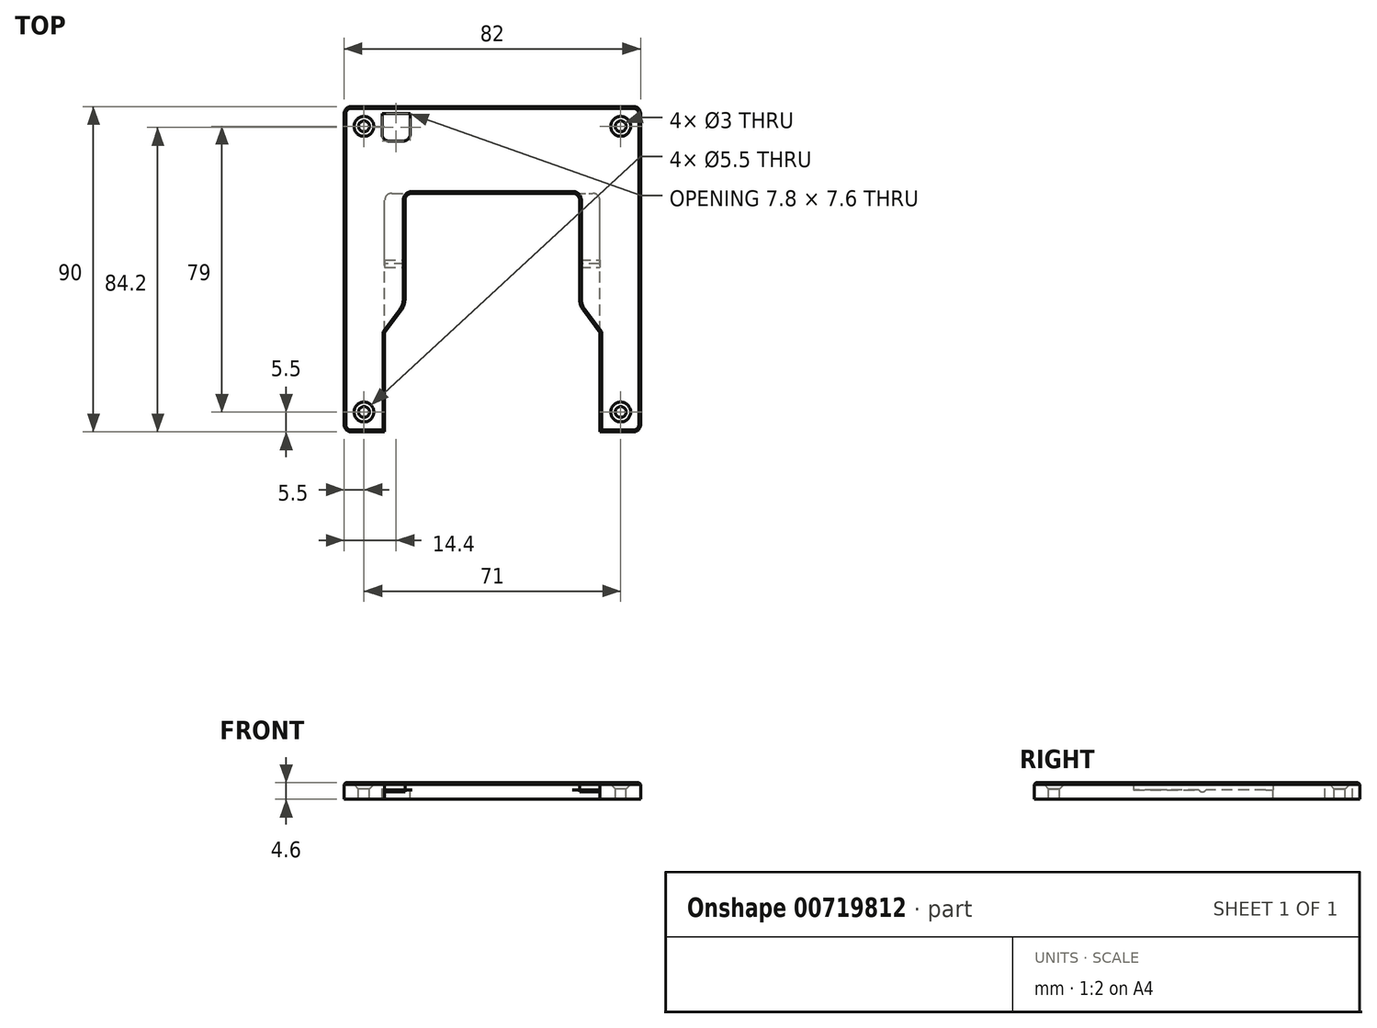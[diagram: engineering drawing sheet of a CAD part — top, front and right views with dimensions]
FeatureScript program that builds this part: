
annotation { "Feature Type Name" : "Feature", "Feature Type Description" : "" }
export const myFeature = defineFeature(function(context is Context, id is Id, definition is map)
    precondition{}
    {
        {
            var Q0;
            Q0=qCreatedBy(makeId("Top.planeOp"),FACE);
            var sketch = newSketch(context, id + "F0", { "sketchPlane" : qUnion([Q0])});
            skLineSegment(sketch, "E0.bottom", {"start": v(2, 0) * mm, "end": v(80, 0) * mm});
            skLineSegment(sketch, "E0.top", {"start": v(2, -90) * mm, "end": v(11.25, -90) * mm});
            skLineSegment(sketch, "E0.left", {"start": v(0, -2) * mm, "end": v(0, -88) * mm});
            skLineSegment(sketch, "E0.right", {"start": v(82, -2) * mm, "end": v(82, -88) * mm});
            skPoint(sketch, "E1.visualSharp", {"position": v(0, 0) * mm});
            skArc(sketch, "E1.filletArc", {"start": v(2, 0) * mm, "mid": v(0.59, -0.59) * mm, "end": v(0, -2) * mm});
            skPoint(sketch, "E2.visualSharp", {"position": v(82, 0) * mm});
            skArc(sketch, "E2.filletArc", {"start": v(82, -2) * mm, "mid": v(81.41, -0.59) * mm, "end": v(80, 0) * mm});
            skPoint(sketch, "E3.visualSharp", {"position": v(82, -90) * mm});
            skArc(sketch, "E3.filletArc", {"start": v(80, -90) * mm, "mid": v(81.41, -89.41) * mm, "end": v(82, -88) * mm});
            skPoint(sketch, "E4.visualSharp", {"position": v(0, -90) * mm});
            skArc(sketch, "E4.filletArc", {"start": v(0, -88) * mm, "mid": v(0.59, -89.41) * mm, "end": v(2, -90) * mm});
            skLineSegment(sketch, "E5.top", {"start": v(18.85, -24) * mm, "end": v(63.15, -24) * mm});
            skLineSegment(sketch, "E5.left", {"start": v(11.25, -90) * mm, "end": v(11.25, -62.5) * mm});
            skLineSegment(sketch, "E5.right", {"start": v(70.75, -90) * mm, "end": v(70.75, -62.5) * mm});
            skLineSegment(sketch, "E6.trimOffspring", {"start": v(70.75, -90) * mm, "end": v(80, -90) * mm});
            skLineSegment(sketch, "E7.right", {"start": v(16.85, -26) * mm, "end": v(16.85, -53.34) * mm});
            skLineSegment(sketch, "E8.right", {"start": v(65.15, -26) * mm, "end": v(65.15, -53.34) * mm});
            skPoint(sketch, "E9.visualSharp", {"position": v(16.85, -24) * mm});
            skArc(sketch, "E9.filletArc", {"start": v(18.85, -24) * mm, "mid": v(17.44, -24.59) * mm, "end": v(16.85, -26) * mm});
            skPoint(sketch, "E10.visualSharp", {"position": v(65.15, -24) * mm});
            skArc(sketch, "E10.filletArc", {"start": v(65.15, -26) * mm, "mid": v(64.56, -24.59) * mm, "end": v(63.15, -24) * mm});
            skPoint(sketch, "E11", {"position": v(16.85, -55) * mm});
            skLineSegment(sketch, "E12", {"start": v(11.25, -62.5) * mm, "end": v(15.86, -56.33) * mm});
            skLineSegment(sketch, "E13", {"start": v(66.14, -56.33) * mm, "end": v(70.75, -62.5) * mm});
            skArc(sketch, "E14.filletArc", {"start": v(15.86, -56.33) * mm, "mid": v(16.6, -54.92) * mm, "end": v(16.85, -53.34) * mm});
            skPoint(sketch, "E15.visualSharp", {"position": v(65.15, -55) * mm});
            skArc(sketch, "E15.filletArc", {"start": v(65.15, -53.34) * mm, "mid": v(65.4, -54.92) * mm, "end": v(66.14, -56.33) * mm});
            skSolve(sketch);
        }
        {
            var Q0;
            Q0=makeQuery(id+"F0.imprint","IMPRINT",FACE,{"disambiguationData":[TD([[makeQuery(id+"F0.imprint","IMPRINT",EDGE,{"derivedFrom":sQuery(id+"F0.wireOp",EDGE,"E0.bottom")}),-1.0]])]});
            extrude(context, id + "F1", {"entities" : qUnion([Q0]), "depth" : 2 * mm, "offsetDistance" : 25 * mm});
        }
        {
            var Q0;
            Q0=makeQuery(id+"F1.opExtrude","CAP_FACE",FACE,{"disambiguationData":[OSD([sQuery(id+"F0.wireOp",EDGE,"E0.bottom"),sQuery(id+"F0.wireOp",EDGE,"E0.top"),sQuery(id+"F0.wireOp",EDGE,"E0.left"),sQuery(id+"F0.wireOp",EDGE,"E0.right"),sQuery(id+"F0.wireOp",EDGE,"E1.filletArc"),sQuery(id+"F0.wireOp",EDGE,"E2.filletArc"),sQuery(id+"F0.wireOp",EDGE,"E3.filletArc"),sQuery(id+"F0.wireOp",EDGE,"E4.filletArc"),sQuery(id+"F0.wireOp",EDGE,"E5.top"),sQuery(id+"F0.wireOp",EDGE,"E5.left"),sQuery(id+"F0.wireOp",EDGE,"E5.right"),sQuery(id+"F0.wireOp",EDGE,"E6.trimOffspring"),sQuery(id+"F0.wireOp",EDGE,"E7.right"),sQuery(id+"F0.wireOp",EDGE,"E8.right"),sQuery(id+"F0.wireOp",EDGE,"E9.filletArc"),sQuery(id+"F0.wireOp",EDGE,"E10.filletArc"),sQuery(id+"F0.wireOp",EDGE,"E12"),sQuery(id+"F0.wireOp",EDGE,"E13"),sQuery(id+"F0.wireOp",EDGE,"E14.filletArc"),sQuery(id+"F0.wireOp",EDGE,"E15.filletArc")])],"isStart":true});
            var sketch = newSketch(context, id + "F2", { "sketchPlane" : qUnion([Q0])});
            skArc(sketch, "E16.0", {"start": v(82, 2) * mm, "mid": v(81.41, 0.59) * mm, "end": v(80, 0) * mm});
            skLineSegment(sketch, "E16.1", {"start": v(2, 0) * mm, "end": v(80, 0) * mm});
            skArc(sketch, "E16.2", {"start": v(2, 0) * mm, "mid": v(0.59, 0.59) * mm, "end": v(0, 2) * mm});
            skLineSegment(sketch, "E16.3", {"start": v(0, 2) * mm, "end": v(0, 88) * mm});
            skArc(sketch, "E16.4", {"start": v(0, 88) * mm, "mid": v(0.59, 89.41) * mm, "end": v(2, 90) * mm});
            skLineSegment(sketch, "E16.5", {"start": v(82, 2) * mm, "end": v(82, 88) * mm});
            skLineSegment(sketch, "E16.6", {"start": v(2, 90) * mm, "end": v(11.25, 90) * mm});
            skLineSegment(sketch, "E16.7", {"start": v(11.25, 90) * mm, "end": v(11.25, 62.5) * mm});
            skLineSegment(sketch, "E16.9", {"start": v(70.75, 90) * mm, "end": v(70.75, 62.5) * mm});
            skLineSegment(sketch, "E16.10", {"start": v(70.75, 90) * mm, "end": v(80, 90) * mm});
            skArc(sketch, "E16.11", {"start": v(80, 90) * mm, "mid": v(81.41, 89.41) * mm, "end": v(82, 88) * mm});
            skLineSegment(sketch, "E16.14", {"start": v(16.85, 24) * mm, "end": v(65.15, 24) * mm});
            skLineSegment(sketch, "E17", {"start": v(70.75, 62.5) * mm, "end": v(70.75, 26) * mm});
            skLineSegment(sketch, "E18", {"start": v(68.75, 24) * mm, "end": v(65.15, 24) * mm});
            skPoint(sketch, "E19.visualSharp", {"position": v(70.75, 24) * mm});
            skArc(sketch, "E19.filletArc", {"start": v(68.75, 24) * mm, "mid": v(70.16, 24.59) * mm, "end": v(70.75, 26) * mm});
            skLineSegment(sketch, "E20", {"start": v(11.25, 62.5) * mm, "end": v(11.25, 26) * mm});
            skLineSegment(sketch, "E21", {"start": v(13.25, 24) * mm, "end": v(16.85, 24) * mm});
            skPoint(sketch, "E22.visualSharp", {"position": v(11.25, 24) * mm});
            skArc(sketch, "E22.filletArc", {"start": v(11.25, 26) * mm, "mid": v(11.84, 24.59) * mm, "end": v(13.25, 24) * mm});
            skSolve(sketch);
        }
        {
            var Q0;
            Q0 = qSketchRegion(id + "F2", true);
            extrude(context, id + "F3", {"entities" : qUnion([Q0]), "operationType" : NewBodyOperationType.ADD, "depth" : 2.2 * mm, "offsetDistance" : 25 * mm});
        }
        {
            var Q0;
            Q0=makeQuery(id+"F1.opExtrude","CAP_FACE",FACE,{"disambiguationData":[OSD([sQuery(id+"F0.wireOp",EDGE,"E0.bottom"),sQuery(id+"F0.wireOp",EDGE,"E0.top"),sQuery(id+"F0.wireOp",EDGE,"E0.left"),sQuery(id+"F0.wireOp",EDGE,"E0.right"),sQuery(id+"F0.wireOp",EDGE,"E1.filletArc"),sQuery(id+"F0.wireOp",EDGE,"E2.filletArc"),sQuery(id+"F0.wireOp",EDGE,"E3.filletArc"),sQuery(id+"F0.wireOp",EDGE,"E4.filletArc"),sQuery(id+"F0.wireOp",EDGE,"E5.top"),sQuery(id+"F0.wireOp",EDGE,"E5.left"),sQuery(id+"F0.wireOp",EDGE,"E5.right"),sQuery(id+"F0.wireOp",EDGE,"E6.trimOffspring"),sQuery(id+"F0.wireOp",EDGE,"E7.right"),sQuery(id+"F0.wireOp",EDGE,"E8.right"),sQuery(id+"F0.wireOp",EDGE,"E9.filletArc"),sQuery(id+"F0.wireOp",EDGE,"E10.filletArc"),sQuery(id+"F0.wireOp",EDGE,"E12"),sQuery(id+"F0.wireOp",EDGE,"E13"),sQuery(id+"F0.wireOp",EDGE,"E14.filletArc"),sQuery(id+"F0.wireOp",EDGE,"E15.filletArc")])],"isStart":false});
            var sketch = newSketch(context, id + "F4", { "sketchPlane" : qUnion([Q0])});
            skLineSegment(sketch, "E23.bottom", {"start": v(10.5, -2) * mm, "end": v(18.3, -2) * mm});
            skLineSegment(sketch, "E23.top", {"start": v(12.5, -9.6) * mm, "end": v(16.3, -9.6) * mm});
            skLineSegment(sketch, "E23.left", {"start": v(10.5, -2) * mm, "end": v(10.5, -7.6) * mm});
            skLineSegment(sketch, "E23.right", {"start": v(18.3, -2) * mm, "end": v(18.3, -7.6) * mm});
            skPoint(sketch, "E24.visualSharp", {"position": v(10.5, -9.6) * mm});
            skArc(sketch, "E24.filletArc", {"start": v(10.5, -7.6) * mm, "mid": v(11.09, -9.01) * mm, "end": v(12.5, -9.6) * mm});
            skPoint(sketch, "E25.visualSharp", {"position": v(18.3, -9.6) * mm});
            skArc(sketch, "E25.filletArc", {"start": v(16.3, -9.6) * mm, "mid": v(17.71, -9.01) * mm, "end": v(18.3, -7.6) * mm});
            skSolve(sketch);
        }
        {
            var Q0;
            Q0 = qSketchRegion(id + "F4", true);
            extrude(context, id + "F5", {"entities" : qUnion([Q0]), "operationType" : NewBodyOperationType.REMOVE, "oppositeDirection" : true, "depth" : 25 * mm, "offsetDistance" : 25 * mm});
        }
        {
            var Q0;
            Q0=makeQuery(id+"F1.opExtrude","CAP_FACE",FACE,{"disambiguationData":[OSD([sQuery(id+"F0.wireOp",EDGE,"E0.bottom"),sQuery(id+"F0.wireOp",EDGE,"E0.top"),sQuery(id+"F0.wireOp",EDGE,"E0.left"),sQuery(id+"F0.wireOp",EDGE,"E0.right"),sQuery(id+"F0.wireOp",EDGE,"E1.filletArc"),sQuery(id+"F0.wireOp",EDGE,"E2.filletArc"),sQuery(id+"F0.wireOp",EDGE,"E3.filletArc"),sQuery(id+"F0.wireOp",EDGE,"E4.filletArc"),sQuery(id+"F0.wireOp",EDGE,"E5.top"),sQuery(id+"F0.wireOp",EDGE,"E5.left"),sQuery(id+"F0.wireOp",EDGE,"E5.right"),sQuery(id+"F0.wireOp",EDGE,"E6.trimOffspring"),sQuery(id+"F0.wireOp",EDGE,"E7.right"),sQuery(id+"F0.wireOp",EDGE,"E8.right"),sQuery(id+"F0.wireOp",EDGE,"E9.filletArc"),sQuery(id+"F0.wireOp",EDGE,"E10.filletArc"),sQuery(id+"F0.wireOp",EDGE,"E12"),sQuery(id+"F0.wireOp",EDGE,"E13"),sQuery(id+"F0.wireOp",EDGE,"E14.filletArc"),sQuery(id+"F0.wireOp",EDGE,"E15.filletArc")])],"isStart":false});
            var sketch = newSketch(context, id + "F6", { "sketchPlane" : qUnion([Q0])});
            skCircle(sketch, "E26", {"center": v(5.5, -5.5) * mm, "radius": 1.5 * mm});
            skCircle(sketch, "E27", {"center": v(76.5, -5.5) * mm, "radius": 1.5 * mm});
            skCircle(sketch, "E28", {"center": v(5.5, -84.5) * mm, "radius": 1.5 * mm});
            skCircle(sketch, "E29", {"center": v(76.5, -84.5) * mm, "radius": 1.5 * mm});
            skSolve(sketch);
        }
        {
            var Q0;
            Q0=makeQuery(id+"F6.imprint","IMPRINT",FACE,{"disambiguationData":[TD([[makeQuery(id+"F6.imprint","IMPRINT",EDGE,{"derivedFrom":sQuery(id+"F6.wireOp",EDGE,"E28")}),1.0]])]});
            var Q1;
            Q1=makeQuery(id+"F6.imprint","IMPRINT",FACE,{"disambiguationData":[TD([[makeQuery(id+"F6.imprint","IMPRINT",EDGE,{"derivedFrom":sQuery(id+"F6.wireOp",EDGE,"E29")}),1.0]])]});
            var Q2;
            Q2=makeQuery(id+"F6.imprint","IMPRINT",FACE,{"disambiguationData":[TD([[makeQuery(id+"F6.imprint","IMPRINT",EDGE,{"derivedFrom":sQuery(id+"F6.wireOp",EDGE,"E26")}),1.0]])]});
            var Q3;
            Q3=makeQuery(id+"F6.imprint","IMPRINT",FACE,{"disambiguationData":[TD([[makeQuery(id+"F6.imprint","IMPRINT",EDGE,{"derivedFrom":sQuery(id+"F6.wireOp",EDGE,"E27")}),1.0]])]});
            extrude(context, id + "F7", {"entities" : qUnion([Q0, Q1, Q2, Q3]), "operationType" : NewBodyOperationType.REMOVE, "oppositeDirection" : true, "depth" : 4.2 * mm, "offsetDistance" : 25 * mm});
        }
        {
            var Q0;
            Q0=makeQuery(id+"F1.opExtrude","CAP_FACE",FACE,{"disambiguationData":[OSD([sQuery(id+"F0.wireOp",EDGE,"E0.bottom"),sQuery(id+"F0.wireOp",EDGE,"E0.top"),sQuery(id+"F0.wireOp",EDGE,"E0.left"),sQuery(id+"F0.wireOp",EDGE,"E0.right"),sQuery(id+"F0.wireOp",EDGE,"E1.filletArc"),sQuery(id+"F0.wireOp",EDGE,"E2.filletArc"),sQuery(id+"F0.wireOp",EDGE,"E3.filletArc"),sQuery(id+"F0.wireOp",EDGE,"E4.filletArc"),sQuery(id+"F0.wireOp",EDGE,"E5.top"),sQuery(id+"F0.wireOp",EDGE,"E5.left"),sQuery(id+"F0.wireOp",EDGE,"E5.right"),sQuery(id+"F0.wireOp",EDGE,"E6.trimOffspring"),sQuery(id+"F0.wireOp",EDGE,"E7.right"),sQuery(id+"F0.wireOp",EDGE,"E8.right"),sQuery(id+"F0.wireOp",EDGE,"E9.filletArc"),sQuery(id+"F0.wireOp",EDGE,"E10.filletArc"),sQuery(id+"F0.wireOp",EDGE,"E12"),sQuery(id+"F0.wireOp",EDGE,"E13"),sQuery(id+"F0.wireOp",EDGE,"E14.filletArc"),sQuery(id+"F0.wireOp",EDGE,"E15.filletArc")])],"isStart":false});
            var sketch = newSketch(context, id + "F8", { "sketchPlane" : qUnion([Q0])});
            skCircle(sketch, "E30", {"center": v(5.5, -5.5) * mm, "radius": 2.75 * mm});
            skCircle(sketch, "E31", {"center": v(76.5, -5.5) * mm, "radius": 2.75 * mm});
            skCircle(sketch, "E32", {"center": v(76.5, -84.5) * mm, "radius": 2.75 * mm});
            skCircle(sketch, "E33", {"center": v(5.5, -84.5) * mm, "radius": 2.75 * mm});
            skSolve(sketch);
        }
        {
            var Q0;
            Q0 = qSketchRegion(id + "F8", true);
            extrude(context, id + "F9", {"entities" : qUnion([Q0]), "operationType" : NewBodyOperationType.REMOVE, "oppositeDirection" : true, "depth" : 2 * mm, "offsetDistance" : 25 * mm});
        }
        {
            var Q0;
            Q0=makeQuery(id+"F9.boolean.opBoolean","COPY",EDGE,{"derivedFrom":makeQuery(id+"F9.opExtrude","CAP_EDGE",EDGE,{"disambiguationData":[OSD([sQuery(id+"F8.wireOp",EDGE,"E33")])],"isStart":false})});
            var Q1;
            Q1=makeQuery(id+"F9.boolean.opBoolean","COPY",EDGE,{"derivedFrom":makeQuery(id+"F9.opExtrude","CAP_EDGE",EDGE,{"disambiguationData":[OSD([sQuery(id+"F8.wireOp",EDGE,"E32")])],"isStart":false})});
            var Q2;
            Q2=makeQuery(id+"F9.boolean.opBoolean","COPY",EDGE,{"derivedFrom":makeQuery(id+"F9.opExtrude","CAP_EDGE",EDGE,{"disambiguationData":[OSD([sQuery(id+"F8.wireOp",EDGE,"E30")])],"isStart":false})});
            var Q3;
            Q3=makeQuery(id+"F9.boolean.opBoolean","COPY",EDGE,{"derivedFrom":makeQuery(id+"F9.opExtrude","CAP_EDGE",EDGE,{"disambiguationData":[OSD([sQuery(id+"F8.wireOp",EDGE,"E31")])],"isStart":false})});
            chamfer(context, id + "F10", {"entities" : qUnion([Q0, Q1, Q2, Q3]), "width" : 1.5 * mm, "tangentPropagation" : true});
        }
        {
            var Q0;
            {var subQ0=sQuery(id+"F0.wireOp",EDGE,"E7.right");var subQ1=sQuery(id+"F0.wireOp",EDGE,"E9.filletArc");var subQ2=sQuery(id+"F0.wireOp",EDGE,"E5.left");var subQ3=sQuery(id+"F0.wireOp",EDGE,"E5.top");var subQ4=sQuery(id+"F0.wireOp",EDGE,"E12");var subQ5=sQuery(id+"F0.wireOp",EDGE,"E14.filletArc");Q0=makeQuery(id+"F3.boolean.opBoolean","SPLIT",FACE,{"disambiguationData":[TD([makeQuery(id+"F1.opExtrude","SWEPT_FACE",FACE,{"disambiguationData":[OSD([subQ2])]})])],"derivedFrom":makeQuery(id+"F1.opExtrude","CAP_FACE",FACE,{"disambiguationData":[OSD([sQuery(id+"F0.wireOp",EDGE,"E0.bottom"),sQuery(id+"F0.wireOp",EDGE,"E0.top"),sQuery(id+"F0.wireOp",EDGE,"E0.left"),sQuery(id+"F0.wireOp",EDGE,"E0.right"),sQuery(id+"F0.wireOp",EDGE,"E1.filletArc"),sQuery(id+"F0.wireOp",EDGE,"E2.filletArc"),sQuery(id+"F0.wireOp",EDGE,"E3.filletArc"),sQuery(id+"F0.wireOp",EDGE,"E4.filletArc"),subQ3,subQ2,sQuery(id+"F0.wireOp",EDGE,"E5.right"),sQuery(id+"F0.wireOp",EDGE,"E6.trimOffspring"),subQ0,sQuery(id+"F0.wireOp",EDGE,"E8.right"),subQ1,sQuery(id+"F0.wireOp",EDGE,"E10.filletArc"),subQ4,sQuery(id+"F0.wireOp",EDGE,"E13"),subQ5,sQuery(id+"F0.wireOp",EDGE,"E15.filletArc")])],"isStart":true})});}
            var sketch = newSketch(context, id + "F11", { "sketchPlane" : qUnion([Q0])});
            skLineSegment(sketch, "E34.bottom", {"start": v(11.25, 44.5) * mm, "end": v(16.85, 44.5) * mm});
            skLineSegment(sketch, "E34.top", {"start": v(11.25, 42.5) * mm, "end": v(16.85, 42.5) * mm});
            skLineSegment(sketch, "E34.left", {"start": v(11.25, 44.5) * mm, "end": v(11.25, 42.5) * mm});
            skLineSegment(sketch, "E34.right", {"start": v(16.85, 44.5) * mm, "end": v(16.85, 42.5) * mm});
            skLineSegment(sketch, "E35.bottom", {"start": v(65.15, 42.5) * mm, "end": v(70.75, 42.5) * mm});
            skLineSegment(sketch, "E35.top", {"start": v(65.15, 44.5) * mm, "end": v(70.75, 44.5) * mm});
            skLineSegment(sketch, "E35.left", {"start": v(65.15, 42.5) * mm, "end": v(65.15, 44.5) * mm});
            skLineSegment(sketch, "E35.right", {"start": v(70.75, 42.5) * mm, "end": v(70.75, 44.5) * mm});
            skSolve(sketch);
        }
        {
            var Q0;
            Q0 = qSketchRegion(id + "F11", true);
            extrude(context, id + "F12", {"entities" : qUnion([Q0]), "operationType" : NewBodyOperationType.ADD, "depth" : 0.6 * mm, "offsetDistance" : 25 * mm});
        }
        {
            var Q0;
            Q0=makeQuery(id+"F12.opExtrude","CAP_EDGE",EDGE,{"disambiguationData":[OSD([sQuery(id+"F11.wireOp",EDGE,"E34.top")])],"isStart":false});
            var Q1;
            Q1=makeQuery(id+"F12.opExtrude","CAP_EDGE",EDGE,{"disambiguationData":[OSD([sQuery(id+"F11.wireOp",EDGE,"E34.bottom")])],"isStart":false});
            var Q2;
            Q2=makeQuery(id+"F12.opExtrude","CAP_EDGE",EDGE,{"disambiguationData":[OSD([sQuery(id+"F11.wireOp",EDGE,"E35.bottom")])],"isStart":false});
            var Q3;
            Q3=makeQuery(id+"F12.opExtrude","CAP_EDGE",EDGE,{"disambiguationData":[OSD([sQuery(id+"F11.wireOp",EDGE,"E35.top")])],"isStart":false});
            fillet(context, id + "F13", {"entities" : qUnion([Q0, Q1, Q2, Q3]), "radius" : 1.4 * mm, "tangentPropagation" : true, "allowEdgeOverflow" : false});
        }
        {
            var Q0;
            Q0=makeQuery(id+"F1.opExtrude","CAP_EDGE",EDGE,{"disambiguationData":[OSD([sQuery(id+"F0.wireOp",EDGE,"E1.filletArc")])],"isStart":false});
            var Q1;
            Q1=makeQuery(id+"F1.opExtrude","CAP_EDGE",EDGE,{"disambiguationData":[OSD([sQuery(id+"F0.wireOp",EDGE,"E0.bottom")])],"isStart":false});
            var Q2;
            Q2=makeQuery(id+"F1.opExtrude","CAP_EDGE",EDGE,{"disambiguationData":[OSD([sQuery(id+"F0.wireOp",EDGE,"E0.left")])],"isStart":false});
            var Q3;
            Q3=makeQuery(id+"F5.boolean.opBoolean","COPY",EDGE,{"derivedFrom":makeQuery(id+"F5.opExtrude","CAP_EDGE",EDGE,{"disambiguationData":[OSD([sQuery(id+"F4.wireOp",EDGE,"E23.left")])],"isStart":true})});
            var Q4;
            Q4=makeQuery(id+"F5.boolean.opBoolean","COPY",EDGE,{"derivedFrom":makeQuery(id+"F5.opExtrude","CAP_EDGE",EDGE,{"disambiguationData":[OSD([sQuery(id+"F4.wireOp",EDGE,"E23.bottom")])],"isStart":true})});
            var Q5;
            Q5=makeQuery(id+"F5.boolean.opBoolean","COPY",EDGE,{"derivedFrom":makeQuery(id+"F5.opExtrude","CAP_EDGE",EDGE,{"disambiguationData":[OSD([sQuery(id+"F4.wireOp",EDGE,"E23.right")])],"isStart":true})});
            var Q6;
            Q6=makeQuery(id+"F5.boolean.opBoolean","COPY",EDGE,{"derivedFrom":makeQuery(id+"F5.opExtrude","CAP_EDGE",EDGE,{"disambiguationData":[OSD([sQuery(id+"F4.wireOp",EDGE,"E25.filletArc")])],"isStart":true})});
            var Q7;
            Q7=makeQuery(id+"F5.boolean.opBoolean","COPY",EDGE,{"derivedFrom":makeQuery(id+"F5.opExtrude","CAP_EDGE",EDGE,{"disambiguationData":[OSD([sQuery(id+"F4.wireOp",EDGE,"E23.top")])],"isStart":true})});
            var Q8;
            Q8=makeQuery(id+"F5.boolean.opBoolean","COPY",EDGE,{"derivedFrom":makeQuery(id+"F5.opExtrude","CAP_EDGE",EDGE,{"disambiguationData":[OSD([sQuery(id+"F4.wireOp",EDGE,"E24.filletArc")])],"isStart":true})});
            var Q9;
            Q9=makeQuery(id+"F1.opExtrude","CAP_EDGE",EDGE,{"disambiguationData":[OSD([sQuery(id+"F0.wireOp",EDGE,"E2.filletArc")])],"isStart":false});
            var Q10;
            Q10=makeQuery(id+"F1.opExtrude","CAP_EDGE",EDGE,{"disambiguationData":[OSD([sQuery(id+"F0.wireOp",EDGE,"E0.right")])],"isStart":false});
            var Q11;
            Q11=makeQuery(id+"F1.opExtrude","CAP_EDGE",EDGE,{"disambiguationData":[OSD([sQuery(id+"F0.wireOp",EDGE,"E5.left")])],"isStart":false});
            var Q12;
            Q12=makeQuery(id+"F1.opExtrude","CAP_EDGE",EDGE,{"disambiguationData":[OSD([sQuery(id+"F0.wireOp",EDGE,"E0.top")])],"isStart":false});
            var Q13;
            Q13=makeQuery(id+"F1.opExtrude","CAP_EDGE",EDGE,{"disambiguationData":[OSD([sQuery(id+"F0.wireOp",EDGE,"E4.filletArc")])],"isStart":false});
            var Q14;
            Q14=makeQuery(id+"F1.opExtrude","CAP_EDGE",EDGE,{"disambiguationData":[OSD([sQuery(id+"F0.wireOp",EDGE,"E3.filletArc")])],"isStart":false});
            var Q15;
            Q15=makeQuery(id+"F1.opExtrude","CAP_EDGE",EDGE,{"disambiguationData":[OSD([sQuery(id+"F0.wireOp",EDGE,"E6.trimOffspring")])],"isStart":false});
            var Q16;
            Q16=makeQuery(id+"F1.opExtrude","CAP_EDGE",EDGE,{"disambiguationData":[OSD([sQuery(id+"F0.wireOp",EDGE,"E5.right")])],"isStart":false});
            var Q17;
            Q17=makeQuery(id+"F1.opExtrude","CAP_EDGE",EDGE,{"disambiguationData":[OSD([sQuery(id+"F0.wireOp",EDGE,"E13")])],"isStart":false});
            var Q18;
            Q18=makeQuery(id+"F1.opExtrude","CAP_EDGE",EDGE,{"disambiguationData":[OSD([sQuery(id+"F0.wireOp",EDGE,"E15.filletArc")])],"isStart":false});
            var Q19;
            Q19=makeQuery(id+"F1.opExtrude","CAP_EDGE",EDGE,{"disambiguationData":[OSD([sQuery(id+"F0.wireOp",EDGE,"E8.right")])],"isStart":false});
            var Q20;
            Q20=makeQuery(id+"F1.opExtrude","CAP_EDGE",EDGE,{"disambiguationData":[OSD([sQuery(id+"F0.wireOp",EDGE,"E10.filletArc")])],"isStart":false});
            var Q21;
            Q21=makeQuery(id+"F1.opExtrude","CAP_EDGE",EDGE,{"disambiguationData":[OSD([sQuery(id+"F0.wireOp",EDGE,"E5.top")])],"isStart":false});
            var Q22;
            Q22=makeQuery(id+"F1.opExtrude","CAP_EDGE",EDGE,{"disambiguationData":[OSD([sQuery(id+"F0.wireOp",EDGE,"E9.filletArc")])],"isStart":false});
            var Q23;
            Q23=makeQuery(id+"F1.opExtrude","CAP_EDGE",EDGE,{"disambiguationData":[OSD([sQuery(id+"F0.wireOp",EDGE,"E7.right")])],"isStart":false});
            var Q24;
            Q24=makeQuery(id+"F1.opExtrude","CAP_EDGE",EDGE,{"disambiguationData":[OSD([sQuery(id+"F0.wireOp",EDGE,"E14.filletArc")])],"isStart":false});
            var Q25;
            Q25=makeQuery(id+"F1.opExtrude","CAP_EDGE",EDGE,{"disambiguationData":[OSD([sQuery(id+"F0.wireOp",EDGE,"E12")])],"isStart":false});
            chamfer(context, id + "F14", {"entities" : qUnion([Q0, Q1, Q2, Q3, Q4, Q5, Q6, Q7, Q8, Q9, Q10, Q11, Q12, Q13, Q14, Q15, Q16, Q17, Q18, Q19, Q20, Q21, Q22, Q23, Q24, Q25]), "width" : 0.5 * mm, "tangentPropagation" : true});
        }
        {
            var Q0;
            Q0=makeQuery(id+"F3.opExtrude","CAP_FACE",FACE,{"disambiguationData":[OSD([sQuery(id+"F2.wireOp",EDGE,"E16.0"),sQuery(id+"F2.wireOp",EDGE,"E16.1"),sQuery(id+"F2.wireOp",EDGE,"E16.2"),sQuery(id+"F2.wireOp",EDGE,"E16.3"),sQuery(id+"F2.wireOp",EDGE,"E16.4"),sQuery(id+"F2.wireOp",EDGE,"E16.5"),sQuery(id+"F2.wireOp",EDGE,"E16.6"),sQuery(id+"F2.wireOp",EDGE,"E16.7"),sQuery(id+"F2.wireOp",EDGE,"E16.9"),sQuery(id+"F2.wireOp",EDGE,"E16.10"),sQuery(id+"F2.wireOp",EDGE,"E16.11"),sQuery(id+"F2.wireOp",EDGE,"E16.14"),sQuery(id+"F2.wireOp",EDGE,"E17"),sQuery(id+"F2.wireOp",EDGE,"E18"),sQuery(id+"F2.wireOp",EDGE,"E19.filletArc"),sQuery(id+"F2.wireOp",EDGE,"E20"),sQuery(id+"F2.wireOp",EDGE,"E21"),sQuery(id+"F2.wireOp",EDGE,"E22.filletArc")])],"isStart":false});
            extrude(context, id + "F15", {"entities" : qUnion([Q0]), "operationType" : NewBodyOperationType.ADD, "depth" : 0.4 * mm, "offsetDistance" : 25 * mm});
        }
    });
